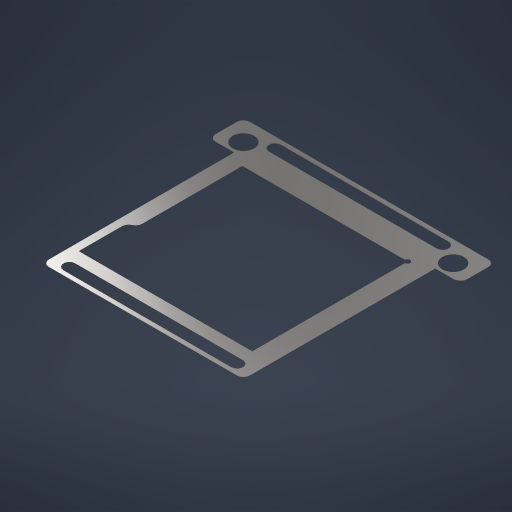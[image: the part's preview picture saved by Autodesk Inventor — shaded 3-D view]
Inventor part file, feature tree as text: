
AUTODESK INVENTOR PART (.ipt)
format: ipt  version: 2024 (Build 280153000, 153)  size: 354,816 bytes
history: native  units: in
note: dims shown in document units (in); Inventor stores cm internally (conversion verified against a paired STEP export)
features: extrude x5, hole x1, fillet x1, sketch x1
ambient origin geometry x8: Origin, YZ Plane, XZ Plane, XY Plane, X Axis, Y Axis, Z Axis, Center Point
bodies: Solid1 (feature_tree)
feature tree (8):
  extrude  "Extrusion1"  Depth=2.7in
  extrude  "Extrusion2"  Depth=0.002in TaperAngle=0.0deg
  extrude  "Extrusion3"  TaperAngle=0.0deg  [1 undecoded]
  hole  "Hole1"  [1 undecoded]
  extrude  "Extrusion4"  Depth=0.4134in
  extrude  "Extrusion5"  Depth=0.1378in
  fillet  "Fillet1"  Radius=0.1378in
  sketch  "Sketch2"  dims[d0=3.0in d1=2.7in d2=0.002in d3=0.0in d7=0.0in d8=0.0in d14=0.3in d16=0.4134in d17=0.1378in d18=0.1378in d19=2.0in d20=2.0in d21=0.125in d22=0.125in d23=1.0in d24=0.0in d27=0.0in d28=0.0in d29=0.0625in d30=0.5906in d31=0.1919in d32=0.096in d33=0.0in d34=0.0in d39=1.8504in d40=1.9685in d41=0.25in d42=0.25in d43=0.25in d44=0.253in d45=0.2362in d46=0.1575in d47=0.0787in d48=90.0deg d49=0.315in d50=0.8108in d51=0.0787in d52=0.075in d53=0.225in d54=0.0295in d55=0.2146in]
note: 2 required parameter values undecoded (feature->parameter linkage not recoverable at this tier; creation-order binding heuristic only, values carry confidence <= 0.55)
